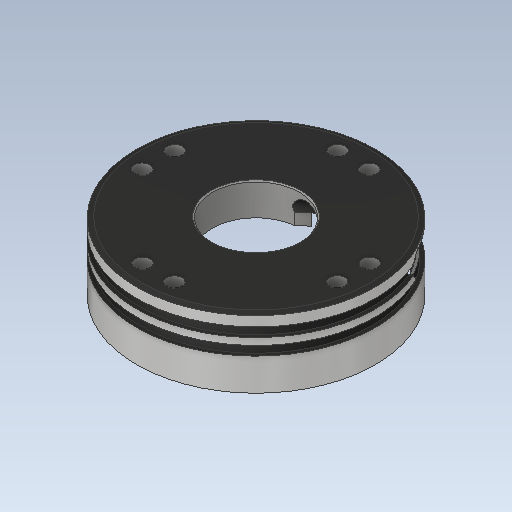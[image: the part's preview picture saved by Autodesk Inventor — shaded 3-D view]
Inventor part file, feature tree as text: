
AUTODESK INVENTOR PART (.ipt)
format: ipt  version: 2020.1 (Build 241239000, 239)  size: 259,584 bytes
history: native  units: mm
features: hole x1
ambient origin geometry x8: Origin, YZ Plane, XZ Plane, XY Plane, X Axis, Y Axis, Z Axis, Center Point
bodies: Solid1 (feature_tree), Body1 (feature_tree)
feature tree (1):
  hole  "Hole Centric Line"  [1 undecoded]
note: 1 required parameter value undecoded (feature->parameter linkage not recoverable at this tier; creation-order binding heuristic only, values carry confidence <= 0.55)
